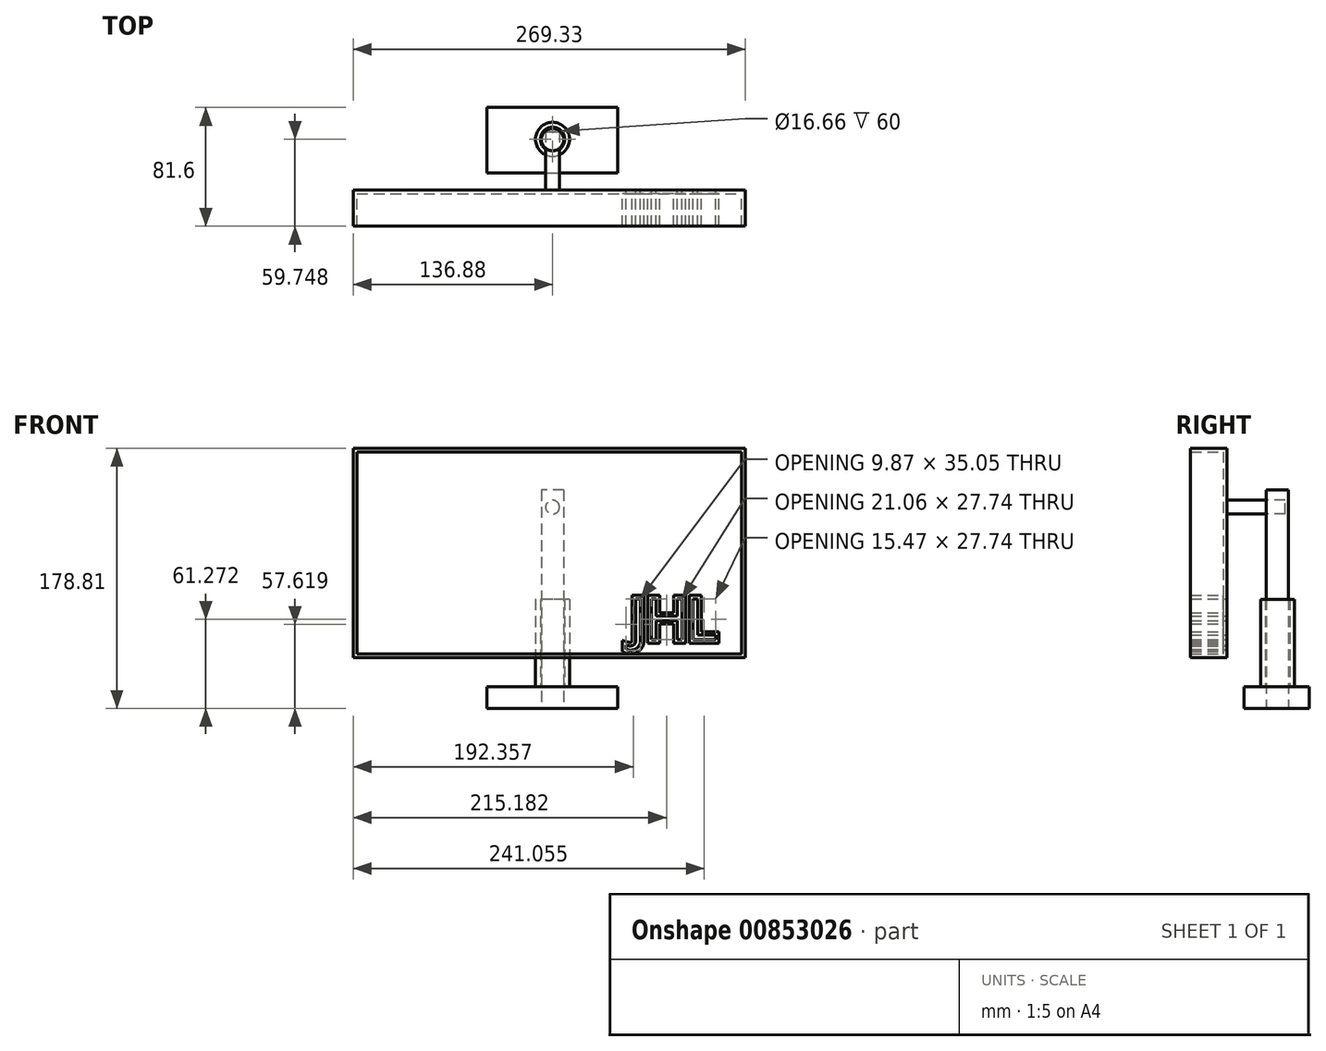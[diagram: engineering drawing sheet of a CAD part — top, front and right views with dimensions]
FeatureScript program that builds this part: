
annotation { "Feature Type Name" : "Feature", "Feature Type Description" : "" }
export const myFeature = defineFeature(function(context is Context, id is Id, definition is map)
    precondition{}
    {
        {
            var Q0;
            Q0=qCreatedBy(makeId("Top.planeOp"),FACE);
            var sketch = newSketch(context, id + "F0", { "sketchPlane" : qUnion([Q0])});
            skLineSegment(sketch, "E0.bottom", {"start": v(-45.18, 56.6) * mm, "end": v(44.79, 56.6) * mm});
            skLineSegment(sketch, "E0.top", {"start": v(-45.18, 11.71) * mm, "end": v(44.79, 11.71) * mm});
            skLineSegment(sketch, "E0.left", {"start": v(-45.18, 56.6) * mm, "end": v(-45.18, 11.71) * mm});
            skLineSegment(sketch, "E0.right", {"start": v(44.79, 56.6) * mm, "end": v(44.79, 11.71) * mm});
            skCircle(sketch, "E1", {"center": v(0, 34.75) * mm, "radius": 11.68 * mm});
            skCircle(sketch, "E2", {"center": v(0, 34.75) * mm, "radius": 8.33 * mm});
            skSolve(sketch);
        }
        {
            var Q0;
            Q0=makeQuery(id+"F0.imprint","IMPRINT",FACE,{"disambiguationData":[TD([[makeQuery(id+"F0.imprint","IMPRINT",EDGE,{"derivedFrom":sQuery(id+"F0.wireOp",EDGE,"E0.bottom")}),-1.0]])]});
            var Q1;
            Q1=makeQuery(id+"F0.imprint","IMPRINT",FACE,{"disambiguationData":[TD([[makeQuery(id+"F0.imprint","IMPRINT",EDGE,{"derivedFrom":sQuery(id+"F0.wireOp",EDGE,"E2")}),1.0]])]});
            var Q2;
            Q2=makeQuery(id+"F0.imprint","IMPRINT",FACE,{"disambiguationData":[TD([[makeQuery(id+"F0.imprint","IMPRINT",EDGE,{"derivedFrom":sQuery(id+"F0.wireOp",EDGE,"E1")}),1.0]])]});
            extrude(context, id + "F1", {"entities" : qUnion([Q0, Q1, Q2]), "depth" : 15 * mm, "offsetDistance" : 25 * mm});
        }
        {
            var Q0;
            Q0=makeQuery(id+"F0.imprint","IMPRINT",FACE,{"disambiguationData":[TD([[makeQuery(id+"F0.imprint","IMPRINT",EDGE,{"derivedFrom":sQuery(id+"F0.wireOp",EDGE,"E1")}),1.0]])]});
            extrude(context, id + "F2", {"entities" : qUnion([Q0]), "operationType" : NewBodyOperationType.ADD, "depth" : 75 * mm, "offsetDistance" : 25 * mm});
        }
        {
            var Q0;
            Q0=qCreatedBy(makeId("Top.planeOp"),FACE);
            var sketch = newSketch(context, id + "F3", { "sketchPlane" : qUnion([Q0])});
            skCircle(sketch, "E3", {"center": v(0, 34.58) * mm, "radius": 7.68 * mm});
            skSolve(sketch);
        }
        {
            var Q0;
            Q0=qSketchRegion(id+"F3",true);
            extrude(context, id + "F4", {"entities" : qUnion([Q0]), "depth" : 150 * mm, "offsetDistance" : 25 * mm});
        }
        {
            var Q0;
            Q0=qCreatedBy(makeId("Front.planeOp"),FACE);
            var sketch = newSketch(context, id + "F5", { "sketchPlane" : qUnion([Q0])});
            skLineSegment(sketch, "E4.bottom", {"start": v(-136.88, 178.8) * mm, "end": v(132.45, 178.8) * mm});
            skLineSegment(sketch, "E4.top", {"start": v(-136.88, 34.99) * mm, "end": v(132.45, 34.99) * mm});
            skLineSegment(sketch, "E4.left", {"start": v(-136.88, 178.8) * mm, "end": v(-136.88, 34.99) * mm});
            skLineSegment(sketch, "E4.right", {"start": v(132.45, 178.8) * mm, "end": v(132.45, 34.99) * mm});
            skText(sketch, "E5", { "text": "JHL", "fontName": "OpenSans-Regular.ttf"});
            skCircle(sketch, "E6", {"center": v(0, 138.34) * mm, "radius": 4.75 * mm});
            const initialGuessF5  = {"E5": [0.05358, 0.0474, 1, 0, 0.02798]};
            skSetInitialGuess(sketch, initialGuessF5);
            skSolve(sketch);
        }
        {
            var Q0;
            Q0=makeQuery(id+"F5.imprint","IMPRINT",FACE,{"disambiguationData":[TD([[makeQuery(id+"F5.imprint","IMPRINT",EDGE,{"derivedFrom":sQuery(id+"F5.wireOp",EDGE,"E5.sketch_text.stroke-22")}),-1.0]])]});
            var Q1;
            Q1=makeQuery(id+"F5.imprint","IMPRINT",FACE,{"disambiguationData":[TD([[makeQuery(id+"F5.imprint","IMPRINT",EDGE,{"derivedFrom":sQuery(id+"F5.wireOp",EDGE,"E5.sketch_text.stroke-10")}),-1.0]])]});
            var Q2;
            Q2=makeQuery(id+"F5.imprint","IMPRINT",FACE,{"disambiguationData":[TD([[makeQuery(id+"F5.imprint","IMPRINT",EDGE,{"derivedFrom":sQuery(id+"F5.wireOp",EDGE,"E5.sketch_text.stroke-0")}),-1.0]])]});
            extrude(context, id + "F6", {"entities" : qUnion([Q0, Q1, Q2]), "depth" : 25 * mm, "offsetDistance" : 25 * mm});
        }
        {
            var Q0;
            Q0=makeQuery(id+"F5.imprint","IMPRINT",FACE,{"disambiguationData":[TD([[makeQuery(id+"F5.imprint","IMPRINT",EDGE,{"derivedFrom":sQuery(id+"F5.wireOp",EDGE,"E4.bottom")}),-1.0]])]});
            var Q1;
            Q1=makeQuery(id+"F5.imprint","IMPRINT",FACE,{"disambiguationData":[TD([[makeQuery(id+"F5.imprint","IMPRINT",EDGE,{"derivedFrom":sQuery(id+"F5.wireOp",EDGE,"E6")}),1.0]])]});
            extrude(context, id + "F7", {"entities" : qUnion([Q0, Q1]), "depth" : 25 * mm, "offsetDistance" : 25 * mm});
        }
        {
            var Q0;
            Q0=makeQuery(id+"F7.opExtrude","CAP_FACE",FACE,{"disambiguationData":[OSD([sQuery(id+"F5.wireOp",EDGE,"E4.bottom"),sQuery(id+"F5.wireOp",EDGE,"E4.top"),sQuery(id+"F5.wireOp",EDGE,"E4.left"),sQuery(id+"F5.wireOp",EDGE,"E4.right"),sQuery(id+"F5.wireOp",EDGE,"E5.sketch_text.stroke-0"),sQuery(id+"F5.wireOp",EDGE,"E5.sketch_text.stroke-1"),sQuery(id+"F5.wireOp",EDGE,"E5.sketch_text.stroke-2"),sQuery(id+"F5.wireOp",EDGE,"E5.sketch_text.stroke-3"),sQuery(id+"F5.wireOp",EDGE,"E5.sketch_text.stroke-4"),sQuery(id+"F5.wireOp",EDGE,"E5.sketch_text.stroke-5"),sQuery(id+"F5.wireOp",EDGE,"E5.sketch_text.stroke-6"),sQuery(id+"F5.wireOp",EDGE,"E5.sketch_text.stroke-7"),sQuery(id+"F5.wireOp",EDGE,"E5.sketch_text.stroke-8"),sQuery(id+"F5.wireOp",EDGE,"E5.sketch_text.stroke-9"),sQuery(id+"F5.wireOp",EDGE,"E5.sketch_text.stroke-10"),sQuery(id+"F5.wireOp",EDGE,"E5.sketch_text.stroke-11"),sQuery(id+"F5.wireOp",EDGE,"E5.sketch_text.stroke-12"),sQuery(id+"F5.wireOp",EDGE,"E5.sketch_text.stroke-13"),sQuery(id+"F5.wireOp",EDGE,"E5.sketch_text.stroke-14"),sQuery(id+"F5.wireOp",EDGE,"E5.sketch_text.stroke-15"),sQuery(id+"F5.wireOp",EDGE,"E5.sketch_text.stroke-16"),sQuery(id+"F5.wireOp",EDGE,"E5.sketch_text.stroke-17"),sQuery(id+"F5.wireOp",EDGE,"E5.sketch_text.stroke-18"),sQuery(id+"F5.wireOp",EDGE,"E5.sketch_text.stroke-19"),sQuery(id+"F5.wireOp",EDGE,"E5.sketch_text.stroke-20"),sQuery(id+"F5.wireOp",EDGE,"E5.sketch_text.stroke-21"),sQuery(id+"F5.wireOp",EDGE,"E5.sketch_text.stroke-22"),sQuery(id+"F5.wireOp",EDGE,"E5.sketch_text.stroke-23"),sQuery(id+"F5.wireOp",EDGE,"E5.sketch_text.stroke-24"),sQuery(id+"F5.wireOp",EDGE,"E5.sketch_text.stroke-25"),sQuery(id+"F5.wireOp",EDGE,"E5.sketch_text.stroke-26"),sQuery(id+"F5.wireOp",EDGE,"E5.sketch_text.stroke-27")])],"isStart":false});
            shell(context, id + "F8", {"entities" : qUnion([Q0]), "thickness" : 2.5 * mm});
        }
        {
            var Q0;
            Q0=makeQuery(id+"F5.imprint","IMPRINT",FACE,{"disambiguationData":[TD([[makeQuery(id+"F5.imprint","IMPRINT",EDGE,{"derivedFrom":sQuery(id+"F5.wireOp",EDGE,"E6")}),1.0]])]});
            extrude(context, id + "F9", {"entities" : qUnion([Q0]), "oppositeDirection" : true, "depth" : 40 * mm, "offsetDistance" : 25 * mm});
        }
        {
            var Q0;
            Q0=makeQuery(id+"F9.opExtrude","SWEPT_BODY",BODY,{"disambiguationData":[OSD([sQuery(id+"F5.wireOp",EDGE,"E6")])]});
            var Q1;
            Q1=makeQuery(id+"F7.opExtrude","SWEPT_BODY",BODY,{"disambiguationData":[OSD([sQuery(id+"F5.wireOp",EDGE,"E4.bottom"),sQuery(id+"F5.wireOp",EDGE,"E4.top"),sQuery(id+"F5.wireOp",EDGE,"E4.left"),sQuery(id+"F5.wireOp",EDGE,"E4.right"),sQuery(id+"F5.wireOp",EDGE,"E5.sketch_text.stroke-0"),sQuery(id+"F5.wireOp",EDGE,"E5.sketch_text.stroke-1"),sQuery(id+"F5.wireOp",EDGE,"E5.sketch_text.stroke-2"),sQuery(id+"F5.wireOp",EDGE,"E5.sketch_text.stroke-3"),sQuery(id+"F5.wireOp",EDGE,"E5.sketch_text.stroke-4"),sQuery(id+"F5.wireOp",EDGE,"E5.sketch_text.stroke-5"),sQuery(id+"F5.wireOp",EDGE,"E5.sketch_text.stroke-6"),sQuery(id+"F5.wireOp",EDGE,"E5.sketch_text.stroke-7"),sQuery(id+"F5.wireOp",EDGE,"E5.sketch_text.stroke-8"),sQuery(id+"F5.wireOp",EDGE,"E5.sketch_text.stroke-9"),sQuery(id+"F5.wireOp",EDGE,"E5.sketch_text.stroke-10"),sQuery(id+"F5.wireOp",EDGE,"E5.sketch_text.stroke-11"),sQuery(id+"F5.wireOp",EDGE,"E5.sketch_text.stroke-12"),sQuery(id+"F5.wireOp",EDGE,"E5.sketch_text.stroke-13"),sQuery(id+"F5.wireOp",EDGE,"E5.sketch_text.stroke-14"),sQuery(id+"F5.wireOp",EDGE,"E5.sketch_text.stroke-15"),sQuery(id+"F5.wireOp",EDGE,"E5.sketch_text.stroke-16"),sQuery(id+"F5.wireOp",EDGE,"E5.sketch_text.stroke-17"),sQuery(id+"F5.wireOp",EDGE,"E5.sketch_text.stroke-18"),sQuery(id+"F5.wireOp",EDGE,"E5.sketch_text.stroke-19"),sQuery(id+"F5.wireOp",EDGE,"E5.sketch_text.stroke-20"),sQuery(id+"F5.wireOp",EDGE,"E5.sketch_text.stroke-21"),sQuery(id+"F5.wireOp",EDGE,"E5.sketch_text.stroke-22"),sQuery(id+"F5.wireOp",EDGE,"E5.sketch_text.stroke-23"),sQuery(id+"F5.wireOp",EDGE,"E5.sketch_text.stroke-24"),sQuery(id+"F5.wireOp",EDGE,"E5.sketch_text.stroke-25"),sQuery(id+"F5.wireOp",EDGE,"E5.sketch_text.stroke-26"),sQuery(id+"F5.wireOp",EDGE,"E5.sketch_text.stroke-27")])]});
            booleanBodies(context, id + "F10", {"operationType" : BooleanOperationType.SUBTRACTION, "tools" : qUnion([Q0]), "targets" : qUnion([Q1]), "keepTools" : true});
        }
    });
